# Revit family: EcoJet NS 10 basic
name_source: partatom
category: Plumbing Fixtures
revit_build: Autodesk Revit 2014 (Build: 20130308_1515(x64)
units: mm (PartAtom-declared; Revit-internal decimal feet)

## types (1)
- 142093 - EcoJet NS 10 basic
    Assembly Code = D2030400
    Cost = 0 $
    Fax = +44 (2) 4747 4040
    Flow rate = 10 L/s out flow of treated effluent to EN 182
    Grease separator body material = Polyethylene
    Grease separator lid material = Polyethylene
    Inlet_Outlet  Connector Dimension = 160 mm  [stored 0.524934 ft]
    Installation guidelines = www.acopassavant.com.au/resources/technical-data
    Maintenance guidelines = www.acopassavant.com.au/resources/installation
    Manufacturer = ACO Polycrete Pty Ltd
    Model = ACO Passavant EcoJet NS 10/ 2000L
    Model Description = Above ground gravity grease separator
    Price = POA - contact ACO
    Product Code = 142093
    Product Dimensions = 2450 x 950 x 1700
    Product Page URL = www.acopassavant.com.au
    Product Standard = EN 1825
    Product Weight = 220 kg
    Product brochure = www.acopassavant.com.au/resources
    Revsion = 0
    Telephone = +61 (0) 2 4747 4000
    Type Comments = ACO Passavant EcoJet NS 10/ 2000L
    URL = www.acopassavant.com.au
    Vent Connector dimension = 110 mm  [stored 0.360892 ft]

note: [stored X ft] marks values corroborated as IEEE doubles in the binary element streams (Revit-internal decimal feet)

## geometry (parser evidence)
native form markers: Sweep x2
no freeform markers — native parametric forms only
